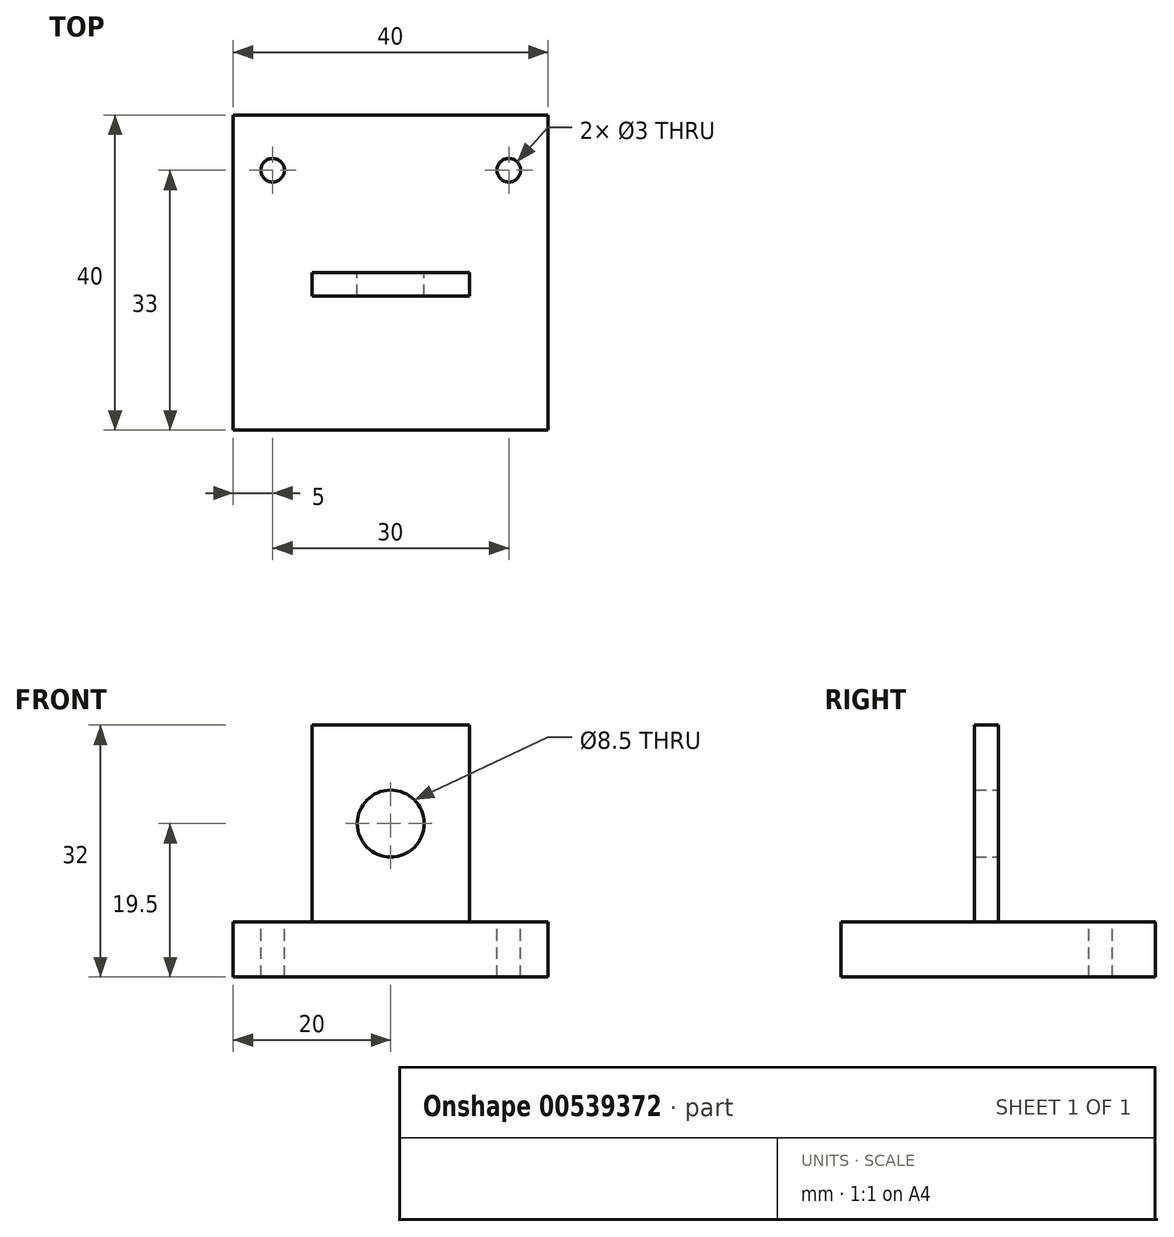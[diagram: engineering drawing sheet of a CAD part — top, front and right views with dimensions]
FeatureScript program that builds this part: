
annotation { "Feature Type Name" : "Feature", "Feature Type Description" : "" }
export const myFeature = defineFeature(function(context is Context, id is Id, definition is map)
    precondition{}
    {
        {
            var Q0;
            Q0=qCreatedBy(makeId("Top.planeOp"),FACE);
            var sketch = newSketch(context, id + "F0", { "sketchPlane" : qUnion([Q0])});
            skLineSegment(sketch, "E0.bottom", {"start": v(-20, 20) * mm, "end": v(20, 20) * mm});
            skLineSegment(sketch, "E0.top", {"start": v(-20, -20) * mm, "end": v(20, -20) * mm});
            skLineSegment(sketch, "E0.left", {"start": v(-20, 20) * mm, "end": v(-20, -20) * mm});
            skLineSegment(sketch, "E0.right", {"start": v(20, 20) * mm, "end": v(20, -20) * mm});
            skSolve(sketch);
        }
        {
            var Q0;
            Q0=makeQuery(id+"F0.imprint","IMPRINT",FACE,{"disambiguationData":[TD([[makeQuery(id+"F0.imprint","IMPRINT",EDGE,{"derivedFrom":sQuery(id+"F0.wireOp",EDGE,"E0.bottom")}),-1.0]])]});
            extrude(context, id + "F1", {"entities" : qUnion([Q0]), "depth" : 7 * mm, "offsetDistance" : 25 * mm});
        }
        {
            var Q0;
            Q0=qCreatedBy(makeId("Top.planeOp"),FACE);
            cPlane(context, id + "F2", {"entities" : qUnion([Q0]), "cplaneType" : CPlaneType.OFFSET, "offset" : 7 * mm, "width" : 150 * mm, "height" : 150 * mm});
        }
        {
            var Q0;
            Q0=qCreatedBy(id+"F2.planeOp",FACE);
            var sketch = newSketch(context, id + "F3", { "sketchPlane" : qUnion([Q0])});
            skLineSegment(sketch, "E1.bottom", {"start": v(-10, 0) * mm, "end": v(10, 0) * mm});
            skLineSegment(sketch, "E1.top", {"start": v(-10, -3) * mm, "end": v(10, -3) * mm});
            skLineSegment(sketch, "E1.left", {"start": v(-10, 0) * mm, "end": v(-10, -3) * mm});
            skLineSegment(sketch, "E1.right", {"start": v(10, 0) * mm, "end": v(10, -3) * mm});
            skSolve(sketch);
        }
        {
            var Q0;
            Q0 = qSketchRegion(id + "F3", true);
            extrude(context, id + "F4", {"entities" : qUnion([Q0]), "operationType" : NewBodyOperationType.ADD, "depth" : 25 * mm, "offsetDistance" : 25 * mm});
        }
        {
            var Q0;
            Q0=qCreatedBy(id+"F2.planeOp",FACE);
            var sketch = newSketch(context, id + "F5", { "sketchPlane" : qUnion([Q0])});
            skCircle(sketch, "E2", {"center": v(-15, 13) * mm, "radius": 1.5 * mm});
            skCircle(sketch, "E3", {"center": v(15, 13) * mm, "radius": 1.5 * mm});
            skSolve(sketch);
        }
        {
            var Q0;
            Q0 = qSketchRegion(id + "F5", true);
            extrude(context, id + "F6", {"entities" : qUnion([Q0]), "operationType" : NewBodyOperationType.REMOVE, "oppositeDirection" : true, "depth" : 25 * mm, "offsetDistance" : 25 * mm});
        }
        {
            var Q0;
            Q0=qCreatedBy(makeId("Front.planeOp"),FACE);
            var sketch = newSketch(context, id + "F7", { "sketchPlane" : qUnion([Q0])});
            skCircle(sketch, "E4", {"center": v(0, 19.5) * mm, "radius": 4.25 * mm});
            skSolve(sketch);
        }
        {
            var Q0;
            Q0 = qSketchRegion(id + "F7", true);
            extrude(context, id + "F8", {"entities" : qUnion([Q0]), "operationType" : NewBodyOperationType.REMOVE, "depth" : 25 * mm, "offsetDistance" : 25 * mm});
        }
    });
